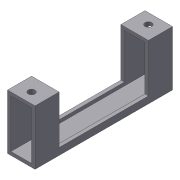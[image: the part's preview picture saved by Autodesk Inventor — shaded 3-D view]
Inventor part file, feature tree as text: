
AUTODESK INVENTOR PART (.ipt)
format: ipt  version: 2012 (Build 160160000, 160)  size: 108,544 bytes
history: native  units: in
note: dims shown in document units (in); Inventor stores cm internally (conversion verified against a paired STEP export)
features: extrude x3, sketch x3, shell x1
ambient origin geometry x8: Origin, YZ Plane, XZ Plane, XY Plane, X Axis, Y Axis, Z Axis, Center Point
bodies: Solid1 (feature_tree)
feature tree (7):
  extrude  "Extrusion1"  Depth=2.0in
  shell  "Shell1"  Thickness=5.0in
  sketch  "Sketch3"  dims[d10=0.25in d11=0.5in d12=0.375in d13=0.5in d14=0.375in d15=5.0in d16=0.0in d17=5.0in d18=0.0in d19=3.25in]
  sketch  "Sketch2"  dims[d4=0.125in d5=0.25in]
  extrude  "Extrusion3"  Depth=0.25in
  extrude  "Extrusion4"  Depth=0.5in
  sketch  "Sketch1"  dims[d0=1.0in d1=2.0in d2=5.0in d3=0.0in]
